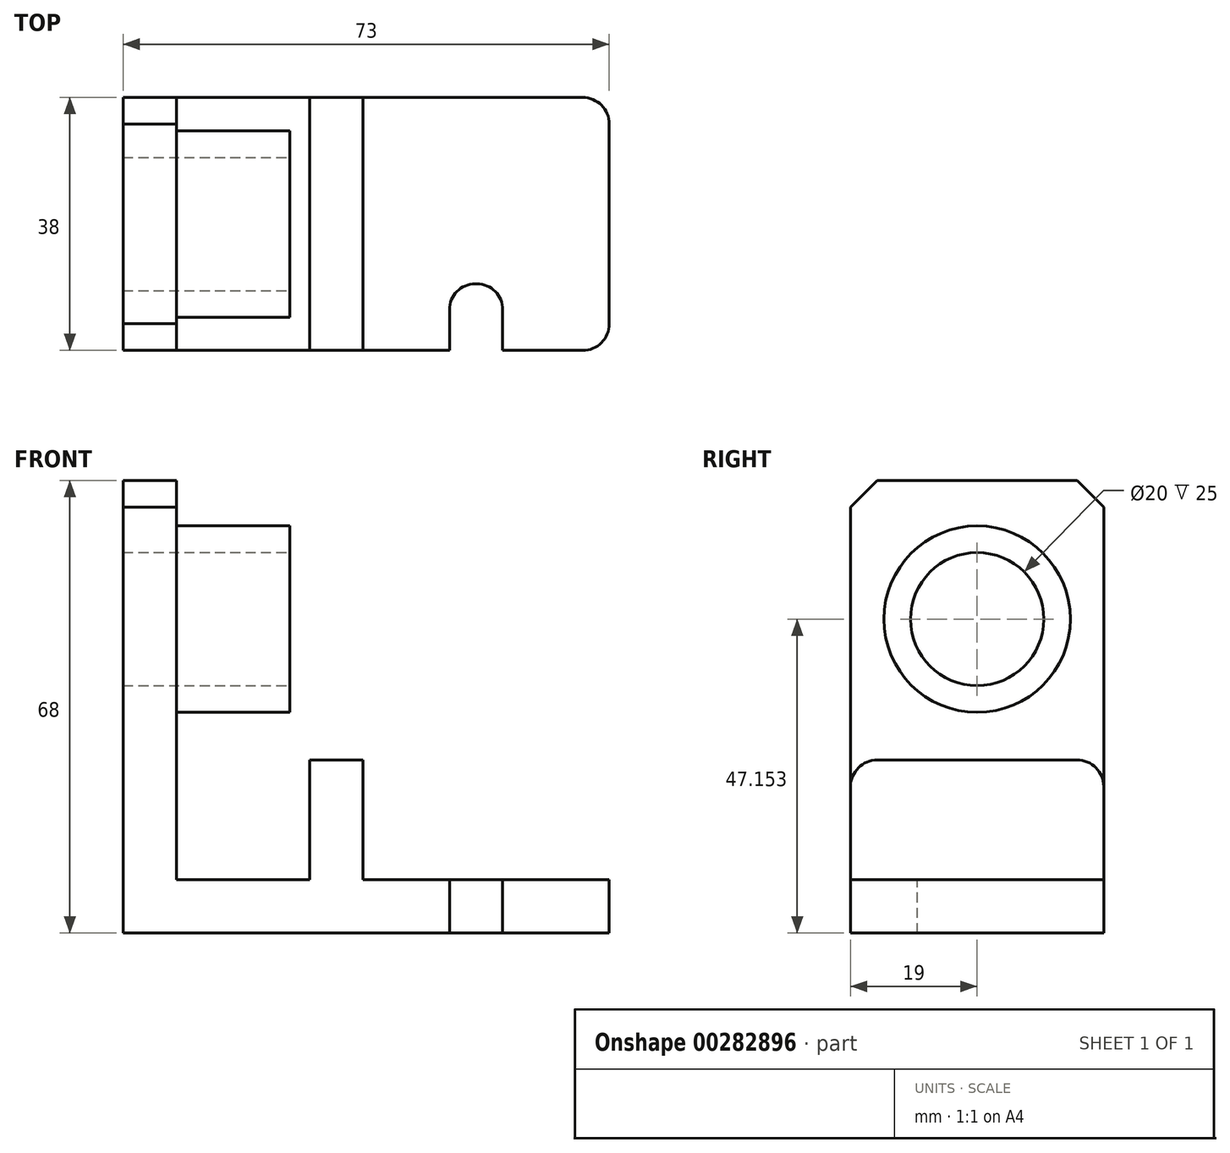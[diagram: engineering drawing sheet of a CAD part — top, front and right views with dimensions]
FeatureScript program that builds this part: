
annotation { "Feature Type Name" : "Feature", "Feature Type Description" : "" }
export const myFeature = defineFeature(function(context is Context, id is Id, definition is map)
    precondition{}
    {
        {
            var Q0;
            Q0=qCreatedBy(makeId("Front.planeOp"),FACE);
            var sketch = newSketch(context, id + "F0", { "sketchPlane" : qUnion([Q0])});
            skLineSegment(sketch, "E0.bottom", {"start": v(4, 34) * mm, "end": v(-4, 34) * mm});
            skLineSegment(sketch, "E0.top", {"start": v(4, -34) * mm, "end": v(-4, -34) * mm});
            skLineSegment(sketch, "E0.left", {"start": v(4, 34) * mm, "end": v(4, -34) * mm});
            skLineSegment(sketch, "E0.right", {"start": v(-4, 34) * mm, "end": v(-4, -34) * mm});
            skPoint(sketch, "E0.middle", {"position": v(0, 0) * mm});
            skSolve(sketch);
        }
        {
            var Q0;
            Q0=makeQuery(id+"F0.imprint","IMPRINT",FACE,{"disambiguationData":[TD([[makeQuery(id+"F0.imprint","IMPRINT",EDGE,{"derivedFrom":sQuery(id+"F0.wireOp",EDGE,"E0.bottom")}),1.0]])]});
            extrude(context, id + "F1", {"entities" : qUnion([Q0]), "oppositeDirection" : true, "depth" : 38 * mm});
        }
        {
            var Q0;
            Q0=makeQuery(id+"F1.opExtrude","CAP_EDGE",EDGE,{"disambiguationData":[OSD([sQuery(id+"F0.wireOp",EDGE,"E0.bottom")])],"isStart":true});
            var Q1;
            Q1=makeQuery(id+"F1.opExtrude","CAP_EDGE",EDGE,{"disambiguationData":[OSD([sQuery(id+"F0.wireOp",EDGE,"E0.bottom")])],"isStart":false});
            chamfer(context, id + "F2", {"entities" : qUnion([Q0, Q1]), "width" : 4 * mm, "tangentPropagation" : true});
        }
        {
            var Q0;
            Q0=makeQuery(id+"F1.opExtrude","SWEPT_FACE",FACE,{"disambiguationData":[OSD([sQuery(id+"F0.wireOp",EDGE,"E0.left")])]});
            var sketch = newSketch(context, id + "F3", { "sketchPlane" : qUnion([Q0])});
            skLineSegment(sketch, "E1.bottom", {"start": v(0, -34) * mm, "end": v(38, -34) * mm});
            skLineSegment(sketch, "E1.top", {"start": v(0, -26) * mm, "end": v(38, -26) * mm});
            skLineSegment(sketch, "E1.left", {"start": v(0, -34) * mm, "end": v(0, -26) * mm});
            skLineSegment(sketch, "E1.right", {"start": v(38, -34) * mm, "end": v(38, -26) * mm});
            skSolve(sketch);
        }
        {
            var Q0;
            Q0=makeQuery(id+"F3.imprint","IMPRINT",FACE,{"disambiguationData":[TD([[makeQuery(id+"F3.imprint","IMPRINT",EDGE,{"derivedFrom":sQuery(id+"F3.wireOp",EDGE,"E1.bottom")}),-1.0]])]});
            extrude(context, id + "F4", {"entities" : qUnion([Q0]), "operationType" : NewBodyOperationType.ADD, "depth" : 65 * mm});
        }
        {
            var Q0;
            Q0=makeQuery(id+"F4.opExtrude","SWEPT_FACE",FACE,{"disambiguationData":[OSD([sQuery(id+"F3.wireOp",EDGE,"E1.top")])]});
            var sketch = newSketch(context, id + "F5", { "sketchPlane" : qUnion([Q0])});
            skLineSegment(sketch, "E2", {"start": v(69, 38) * mm, "end": v(32, 38) * mm});
            skLineSegment(sketch, "E3", {"start": v(32, 38) * mm, "end": v(24, 38) * mm});
            skLineSegment(sketch, "E4", {"start": v(24, 38) * mm, "end": v(24, 0) * mm});
            skLineSegment(sketch, "E5", {"start": v(24, 0) * mm, "end": v(32, 0) * mm});
            skLineSegment(sketch, "E6", {"start": v(32, 0) * mm, "end": v(32, 38) * mm});
            skSolve(sketch);
        }
        {
            var Q0;
            Q0=makeQuery(id+"F5.imprint","IMPRINT",FACE,{"disambiguationData":[TD([[makeQuery(id+"F5.imprint","IMPRINT",EDGE,{"derivedFrom":sQuery(id+"F5.wireOp",EDGE,"E3")}),1.0]])]});
            extrude(context, id + "F6", {"entities" : qUnion([Q0]), "operationType" : NewBodyOperationType.ADD, "depth" : 18 * mm});
        }
        {
            var Q0;
            Q0=makeQuery(id+"F6.opExtrude","CAP_EDGE",EDGE,{"disambiguationData":[OSD([sQuery(id+"F5.wireOp",EDGE,"E5")])],"isStart":false});
            var Q1;
            Q1=makeQuery(id+"F6.opExtrude","CAP_EDGE",EDGE,{"disambiguationData":[OSD([sQuery(id+"F5.wireOp",EDGE,"E3")])],"isStart":false});
            fillet(context, id + "F7", {"entities" : qUnion([Q0, Q1]), "radius" : 4 * mm, "tangentPropagation" : true, "allowEdgeOverflow" : false});
        }
        {
            var Q0;
            Q0=makeQuery(id+"F4.opExtrude","CAP_EDGE",EDGE,{"disambiguationData":[OSD([sQuery(id+"F3.wireOp",EDGE,"E1.right")])],"isStart":false});
            var Q1;
            Q1=makeQuery(id+"F4.opExtrude","CAP_EDGE",EDGE,{"disambiguationData":[OSD([sQuery(id+"F3.wireOp",EDGE,"E1.left")])],"isStart":false});
            fillet(context, id + "F8", {"entities" : qUnion([Q0, Q1]), "radius" : 4 * mm, "tangentPropagation" : true, "allowEdgeOverflow" : false});
        }
        {
            var Q0;
            {var subQ6=sQuery(id+"F3.wireOp",EDGE,"E1.top");Q0=makeQuery(id+"F6.boolean.opBoolean","SPLIT",FACE,{"disambiguationData":[TD([makeQuery(id+"F6.opExtrude","SWEPT_FACE",FACE,{"disambiguationData":[OSD([sQuery(id+"F5.wireOp",EDGE,"E6")])]})])],"derivedFrom":makeQuery(id+"F4.opExtrude","SWEPT_FACE",FACE,{"disambiguationData":[OSD([subQ6])]})});}
            var sketch = newSketch(context, id + "F9", { "sketchPlane" : qUnion([Q0])});
            skLineSegment(sketch, "E7", {"start": v(32, 38) * mm, "end": v(79.53, 38) * mm});
            skLineSegment(sketch, "E8", {"start": v(79.53, 38) * mm, "end": v(69, 38) * mm});
            skLineSegment(sketch, "E9", {"start": v(69, 38) * mm, "end": v(53, 38) * mm});
            skLineSegment(sketch, "E10", {"start": v(53, 38) * mm, "end": v(45, 38) * mm});
            skLineSegment(sketch, "E11", {"start": v(45, 0) * mm, "end": v(45, 38) * mm});
            skLineSegment(sketch, "E12", {"start": v(45, 0) * mm, "end": v(53, 0) * mm});
            skLineSegment(sketch, "E13", {"start": v(53, 38) * mm, "end": v(53, 0) * mm});
            skLineSegment(sketch, "E14", {"start": v(53, 38) * mm, "end": v(53, 28) * mm});
            skLineSegment(sketch, "E15", {"start": v(53, 28) * mm, "end": v(45, 28) * mm});
            skLineSegment(sketch, "E16", {"start": v(45, 28) * mm, "end": v(45, 0) * mm});
            skLineSegment(sketch, "E17", {"start": v(53, 0) * mm, "end": v(53, 10) * mm});
            skLineSegment(sketch, "E18", {"start": v(45, 10) * mm, "end": v(53, 10) * mm});
            skSolve(sketch);
        }
        {
            var Q0;
            Q0=makeQuery(id+"F9.imprint","IMPRINT",FACE,{"disambiguationData":[TD([[makeQuery(id+"F9.imprint","IMPRINT",EDGE,{"derivedFrom":sQuery(id+"F9.wireOp",EDGE,"E10")}),1.0]])]});
            var Q1;
            {var subQ0=sQuery(id+"F9.wireOp",EDGE,"E12");Q1=makeQuery(id+"F9.imprint","IMPRINT",FACE,{"disambiguationData":[TD([[makeQuery(id+"F9.imprint","IMPRINT",EDGE,{"derivedFrom":subQ0}),-1.0]])]});}
            extrude(context, id + "F10", {"entities" : qUnion([Q0, Q1]), "operationType" : NewBodyOperationType.REMOVE, "oppositeDirection" : true, "depth" : 25 * mm});
        }
        {
            var Q0;
            Q0=makeQuery(id+"F10.boolean.opBoolean","COPY",EDGE,{"derivedFrom":makeQuery(id+"F10.opExtrude","SWEPT_EDGE",EDGE,{"disambiguationData":[OSD([sQuery(id+"F9.wireOp",EDGE,"E11"),sQuery(id+"F9.wireOp",EDGE,"E15"),sQuery(id+"F9.wireOp",EDGE,"E16")])]})});
            var Q1;
            Q1=makeQuery(id+"F10.boolean.opBoolean","COPY",EDGE,{"derivedFrom":makeQuery(id+"F10.opExtrude","SWEPT_EDGE",EDGE,{"disambiguationData":[OSD([sQuery(id+"F9.wireOp",EDGE,"E13"),sQuery(id+"F9.wireOp",EDGE,"E14"),sQuery(id+"F9.wireOp",EDGE,"E15")])]})});
            var Q2;
            Q2=makeQuery(id+"F10.boolean.opBoolean","COPY",EDGE,{"derivedFrom":makeQuery(id+"F10.opExtrude","SWEPT_EDGE",EDGE,{"disambiguationData":[OSD([sQuery(id+"F9.wireOp",EDGE,"E16"),sQuery(id+"F9.wireOp",EDGE,"E18")])]})});
            var Q3;
            Q3=makeQuery(id+"F10.boolean.opBoolean","COPY",EDGE,{"derivedFrom":makeQuery(id+"F10.opExtrude","SWEPT_EDGE",EDGE,{"disambiguationData":[OSD([sQuery(id+"F9.wireOp",EDGE,"E13"),sQuery(id+"F9.wireOp",EDGE,"E17"),sQuery(id+"F9.wireOp",EDGE,"E18")])]})});
            fillet(context, id + "F11", {"entities" : qUnion([Q0, Q1, Q2, Q3]), "radius" : 3.86 * mm, "tangentPropagation" : true, "allowEdgeOverflow" : false});
        }
        {
            var Q0;
            Q0=makeQuery(id+"F1.opExtrude","SWEPT_FACE",FACE,{"disambiguationData":[OSD([sQuery(id+"F0.wireOp",EDGE,"E0.left")])]});
            var sketch = newSketch(context, id + "F12", { "sketchPlane" : qUnion([Q0])});
            skCircle(sketch, "E19", {"center": v(19, 13.15) * mm, "radius": 14 * mm});
            skPoint(sketch, "E19.centerSnap0", {"position": v(19, 34) * mm});
            skSolve(sketch);
        }
        {
            var Q0;
            Q0=makeQuery(id+"F12.imprint","IMPRINT",FACE,{"disambiguationData":[TD([[makeQuery(id+"F12.imprint","IMPRINT",EDGE,{"derivedFrom":sQuery(id+"F12.wireOp",EDGE,"E19")}),1.0]])]});
            extrude(context, id + "F13", {"entities" : qUnion([Q0]), "operationType" : NewBodyOperationType.ADD, "depth" : 17 * mm});
        }
        {
            var Q0;
            Q0=makeQuery(id+"F13.opExtrude","CAP_FACE",FACE,{"disambiguationData":[OSD([sQuery(id+"F12.wireOp",EDGE,"E19")])],"isStart":false});
            var sketch = newSketch(context, id + "F14", { "sketchPlane" : qUnion([Q0])});
            skCircle(sketch, "E20", {"center": v(19, 13.15) * mm, "radius": 10 * mm});
            skSolve(sketch);
        }
        {
            var Q0;
            Q0=makeQuery(id+"F14.imprint","IMPRINT",FACE,{"disambiguationData":[TD([[makeQuery(id+"F14.imprint","IMPRINT",EDGE,{"derivedFrom":sQuery(id+"F14.wireOp",EDGE,"E20")}),1.0]])]});
            extrude(context, id + "F15", {"entities" : qUnion([Q0]), "operationType" : NewBodyOperationType.REMOVE, "oppositeDirection" : true, "depth" : 100 * mm});
        }
    });
